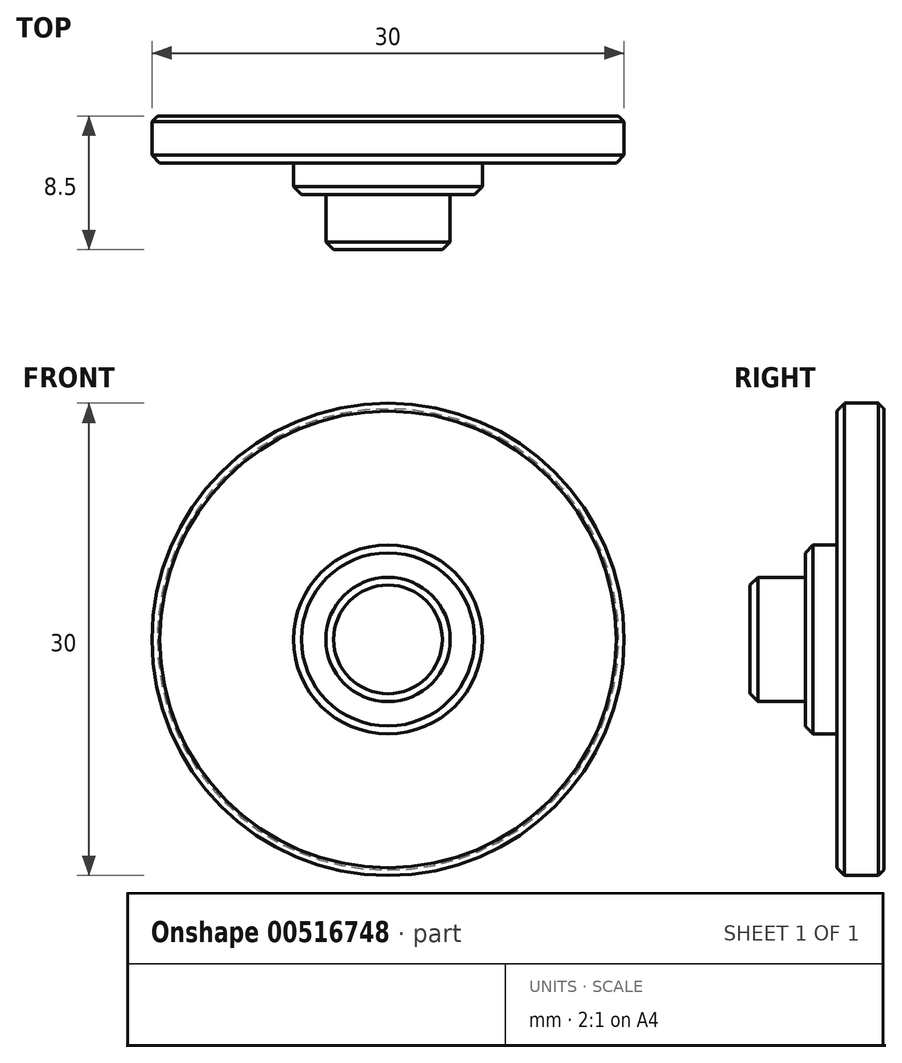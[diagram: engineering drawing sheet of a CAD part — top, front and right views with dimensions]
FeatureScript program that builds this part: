
annotation { "Feature Type Name" : "Feature", "Feature Type Description" : "" }
export const myFeature = defineFeature(function(context is Context, id is Id, definition is map)
    precondition{}
    {
        {
            var Q0;
            Q0=qCreatedBy(makeId("Front.planeOp"),FACE);
            var sketch = newSketch(context, id + "F0", { "sketchPlane" : qUnion([Q0])});
            skCircle(sketch, "E0", {"center": v(0, 0) * mm, "radius": 3.95 * mm});
            skSolve(sketch);
        }
        {
            var Q0;
            Q0 = qSketchRegion(id + "F0", true);
            extrude(context, id + "F1", {"entities" : qUnion([Q0]), "depth" : 3.5 * mm, "offsetDistance" : 25 * mm});
        }
        {
            var Q0;
            Q0=qCreatedBy(makeId("Front.planeOp"),FACE);
            var sketch = newSketch(context, id + "F2", { "sketchPlane" : qUnion([Q0])});
            skCircle(sketch, "E1", {"center": v(0, 0) * mm, "radius": 6 * mm});
            skSolve(sketch);
        }
        {
            var Q0;
            Q0=makeQuery(id+"F2.imprint","IMPRINT",FACE,{"disambiguationData":[TD([[makeQuery(id+"F2.imprint","IMPRINT",EDGE,{"derivedFrom":sQuery(id+"F2.wireOp",EDGE,"E1")}),1.0]])]});
            extrude(context, id + "F3", {"entities" : qUnion([Q0]), "operationType" : NewBodyOperationType.ADD, "oppositeDirection" : true, "depth" : 2 * mm, "offsetDistance" : 25 * mm});
        }
        {
            var Q0;
            Q0=makeQuery(id+"F3.opExtrude","CAP_FACE",FACE,{"disambiguationData":[OSD([sQuery(id+"F2.wireOp",EDGE,"E1")])],"isStart":false});
            var sketch = newSketch(context, id + "F4", { "sketchPlane" : qUnion([Q0])});
            skCircle(sketch, "E2", {"center": v(0, 0) * mm, "radius": 15 * mm});
            skSolve(sketch);
        }
        {
            var Q0;
            Q0 = qSketchRegion(id + "F4", true);
            extrude(context, id + "F5", {"entities" : qUnion([Q0]), "operationType" : NewBodyOperationType.ADD, "depth" : 3 * mm, "offsetDistance" : 25 * mm});
        }
        {
            var Q0;
            Q0=makeQuery(id+"F1.opExtrude","CAP_FACE",FACE,{"disambiguationData":[OSD([sQuery(id+"F0.wireOp",EDGE,"E0")])],"isStart":false});
            chamfer(context, id + "F6", {"entities" : qUnion([Q0]), "width" : 0.5 * mm, "tangentPropagation" : true});
        }
        {
            var Q0;
            Q0=makeQuery(id+"F3.opExtrude","CAP_EDGE",EDGE,{"disambiguationData":[OSD([sQuery(id+"F2.wireOp",EDGE,"E1")])],"isStart":true});
            var Q1;
            Q1=makeQuery(id+"F5.opExtrude","CAP_EDGE",EDGE,{"disambiguationData":[OSD([sQuery(id+"F4.wireOp",EDGE,"E2")])],"isStart":true});
            chamfer(context, id + "F7", {"entities" : qUnion([Q0, Q1]), "width" : 0.5 * mm, "tangentPropagation" : true});
        }
        {
            var Q0;
            Q0=makeQuery(id+"F5.opExtrude","CAP_FACE",FACE,{"disambiguationData":[OSD([sQuery(id+"F4.wireOp",EDGE,"E2")])],"isStart":false});
            chamfer(context, id + "F8", {"entities" : qUnion([Q0]), "chamferType" : ChamferType.OFFSET_ANGLE, "width" : 0.35 * mm, "oppositeDirection" : false, "angle" : 45 * degree, "tangentPropagation" : true});
        }
    });
